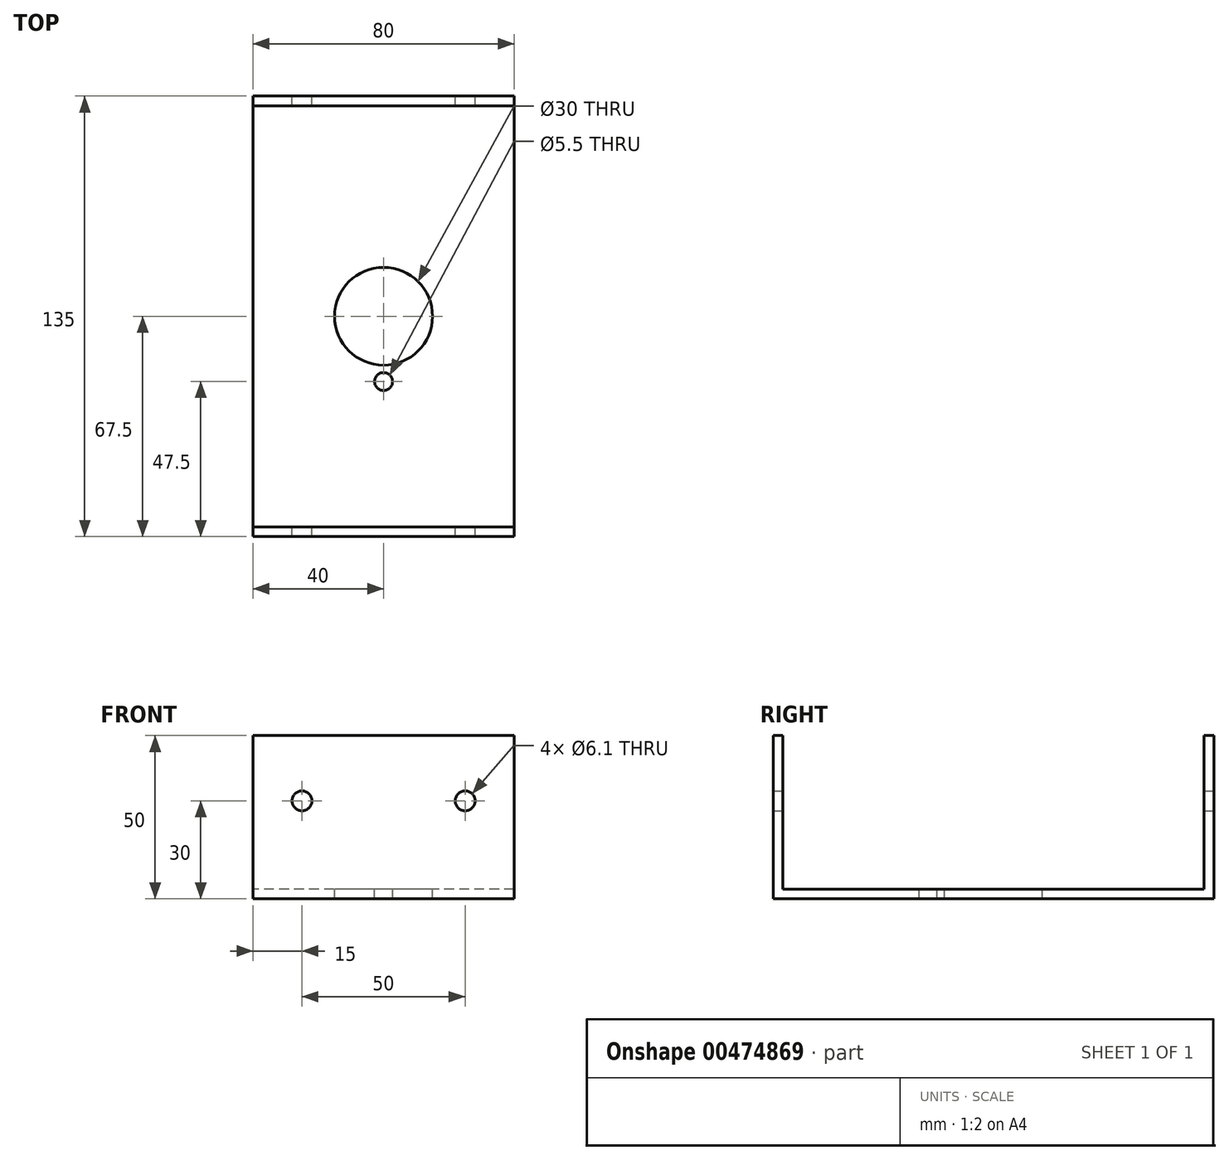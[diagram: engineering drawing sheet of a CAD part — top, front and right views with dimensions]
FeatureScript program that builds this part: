
annotation { "Feature Type Name" : "Feature", "Feature Type Description" : "" }
export const myFeature = defineFeature(function(context is Context, id is Id, definition is map)
    precondition{}
    {
        {
            var Q0;
            Q0=qCreatedBy(makeId("Front.planeOp"),FACE);
            var sketch = newSketch(context, id + "F0", { "sketchPlane" : qUnion([Q0])});
            skLineSegment(sketch, "E0.bottom", {"start": v(0, 0) * mm, "end": v(80, 0) * mm});
            skLineSegment(sketch, "E0.top", {"start": v(0, -50) * mm, "end": v(80, -50) * mm});
            skLineSegment(sketch, "E0.left", {"start": v(0, 0) * mm, "end": v(0, -50) * mm});
            skLineSegment(sketch, "E0.right", {"start": v(80, 0) * mm, "end": v(80, -50) * mm});
            skCircle(sketch, "E1", {"center": v(15, -20) * mm, "radius": 3.05 * mm});
            skCircle(sketch, "E2", {"center": v(65, -20) * mm, "radius": 3.05 * mm});
            skSolve(sketch);
        }
        {
            var Q0;
            Q0=makeQuery(id+"F0.imprint","IMPRINT",FACE,{"disambiguationData":[TD([[makeQuery(id+"F0.imprint","IMPRINT",EDGE,{"derivedFrom":sQuery(id+"F0.wireOp",EDGE,"E0.bottom")}),-1.0]])]});
            extrude(context, id + "F1", {"entities" : qUnion([Q0]), "depth" : 3 * mm});
        }
        {
            var Q0;
            Q0=qCreatedBy(makeId("Front.planeOp"),FACE);
            var sketch = newSketch(context, id + "F2", { "sketchPlane" : qUnion([Q0])});
            skLineSegment(sketch, "E3.bottom", {"start": v(0, -50) * mm, "end": v(80, -50) * mm});
            skLineSegment(sketch, "E3.top", {"start": v(0, -47) * mm, "end": v(80, -47) * mm});
            skLineSegment(sketch, "E3.left", {"start": v(0, -50) * mm, "end": v(0, -47) * mm});
            skLineSegment(sketch, "E3.right", {"start": v(80, -50) * mm, "end": v(80, -47) * mm});
            skSolve(sketch);
        }
        {
            var Q0;
            Q0 = qSketchRegion(id + "F2", true);
            extrude(context, id + "F3", {"entities" : qUnion([Q0]), "operationType" : NewBodyOperationType.ADD, "depth" : 132 * mm, "hasSecondDirection" : true, "secondDirectionOppositeDirection" : true, "secondDirectionDepth" : 0 * mm});
        }
        {
            var Q0;
            Q0 = qSketchRegion(id + "F0", true);
            extrude(context, id + "F4", {"entities" : qUnion([Q0]), "operationType" : NewBodyOperationType.ADD, "depth" : 135 * mm, "hasSecondDirection" : true, "secondDirectionOppositeDirection" : false, "secondDirectionDepth" : 132 * mm});
        }
        {
            var Q0;
            Q0=qCreatedBy(makeId("Top.planeOp"),FACE);
            var sketch = newSketch(context, id + "F5", { "sketchPlane" : qUnion([Q0])});
            skCircle(sketch, "E4", {"center": v(40, -67.5) * mm, "radius": 15 * mm});
            skCircle(sketch, "E5", {"center": v(40, -87.5) * mm, "radius": 2.75 * mm});
            skSolve(sketch);
        }
        {
            var Q0;
            Q0=makeQuery(id+"F5.imprint","IMPRINT",FACE,{"disambiguationData":[TD([[makeQuery(id+"F5.imprint","IMPRINT",EDGE,{"derivedFrom":sQuery(id+"F5.wireOp",EDGE,"E4")}),1.0]])]});
            extrude(context, id + "F6", {"entities" : qUnion([Q0]), "operationType" : NewBodyOperationType.REMOVE, "oppositeDirection" : true, "depth" : 86.5 * mm});
        }
        {
            var Q0;
            Q0=makeQuery(id+"F5.imprint","IMPRINT",FACE,{"disambiguationData":[TD([[makeQuery(id+"F5.imprint","IMPRINT",EDGE,{"derivedFrom":sQuery(id+"F5.wireOp",EDGE,"E5")}),1.0]])]});
            extrude(context, id + "F7", {"entities" : qUnion([Q0]), "operationType" : NewBodyOperationType.REMOVE, "endBound" : BoundingType.THROUGH_ALL, "oppositeDirection" : true, "depth" : 25 * mm});
        }
    });
